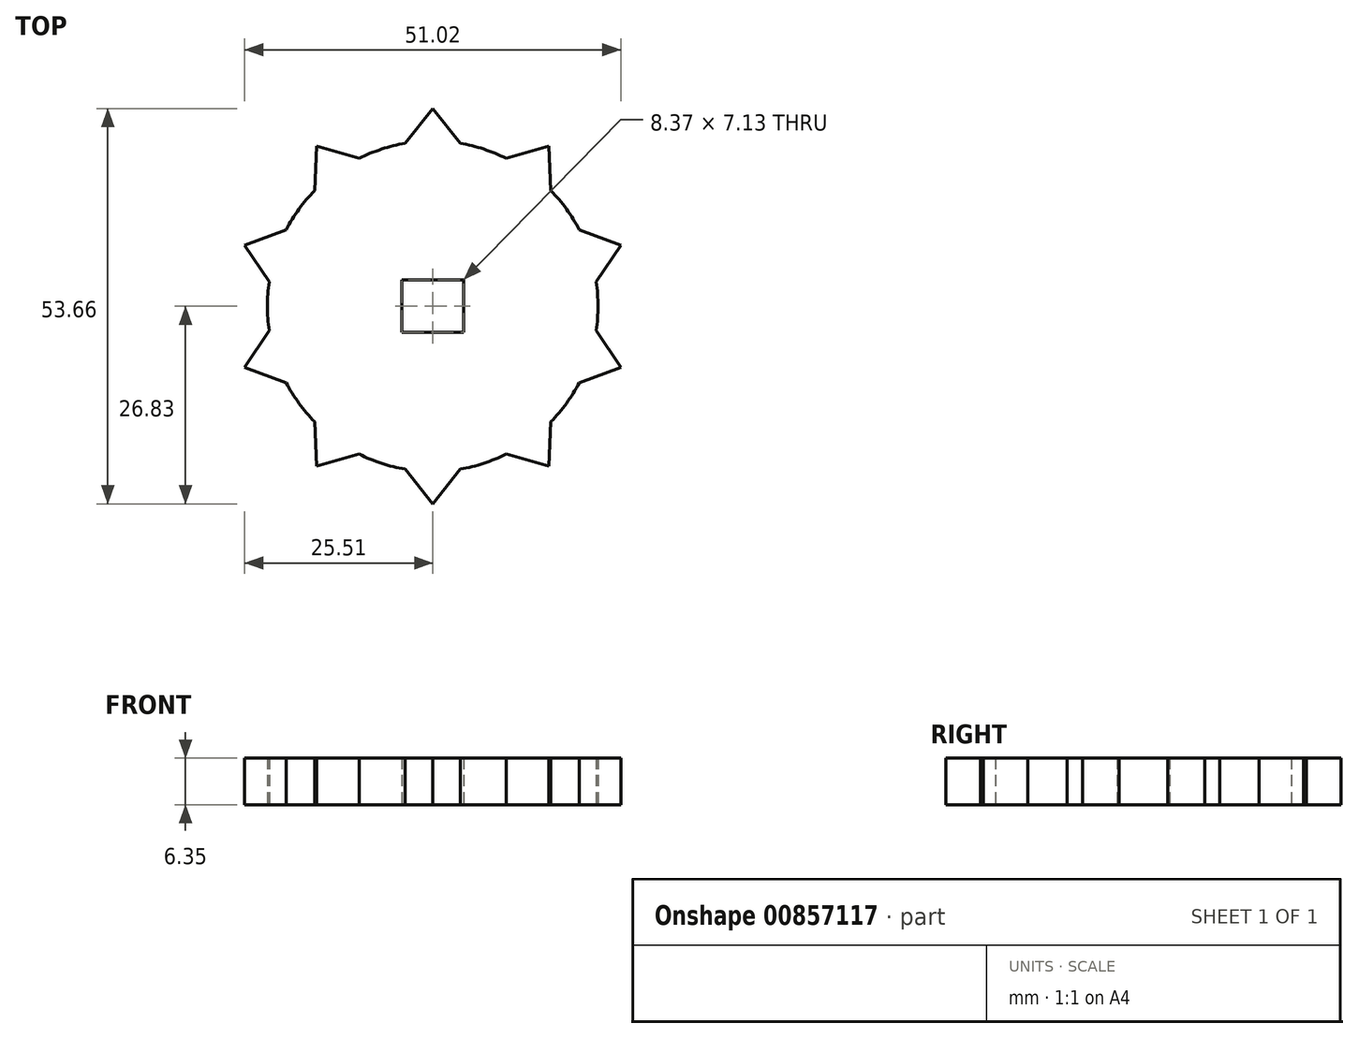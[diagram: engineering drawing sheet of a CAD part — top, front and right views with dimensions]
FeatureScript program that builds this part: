
annotation { "Feature Type Name" : "Feature", "Feature Type Description" : "" }
export const myFeature = defineFeature(function(context is Context, id is Id, definition is map)
    precondition{}
    {
        {
            var Q0;
            Q0=qCreatedBy(makeId("Top.planeOp"),FACE);
            var sketch = newSketch(context, id + "F0", { "sketchPlane" : qUnion([Q0])});
            skCircle(sketch, "E0", {"center": v(0, 0) * mm, "radius": 22.42 * mm});
            skCircle(sketch, "E1", {"center": v(0, 0) * mm, "radius": 8.67 * mm});
            skLineSegment(sketch, "E2.bottom", {"start": v(4.19, -3.57) * mm, "end": v(-4.19, -3.57) * mm});
            skLineSegment(sketch, "E2.top", {"start": v(4.19, 3.57) * mm, "end": v(-4.19, 3.57) * mm});
            skLineSegment(sketch, "E2.left", {"start": v(4.19, -3.57) * mm, "end": v(4.19, 3.57) * mm});
            skLineSegment(sketch, "E2.right", {"start": v(-4.19, -3.57) * mm, "end": v(-4.19, 3.57) * mm});
            skLineSegment(sketch, "E3", {"start": v(-3.72, 22.1) * mm, "end": v(0, 26.83) * mm});
            skLineSegment(sketch, "E4", {"start": v(0, 26.83) * mm, "end": v(3.72, 22.1) * mm});
            skLineSegment(sketch, "E5.1.0", {"start": v(-16, 15.7) * mm, "end": v(-15.77, 21.7) * mm});
            skLineSegment(sketch, "E5.1.1", {"start": v(-15.77, 21.7) * mm, "end": v(-9.98, 20.08) * mm});
            skLineSegment(sketch, "E5.2.0", {"start": v(-22.18, 3.29) * mm, "end": v(-25.51, 8.29) * mm});
            skLineSegment(sketch, "E5.2.1", {"start": v(-25.51, 8.29) * mm, "end": v(-19.88, 10.37) * mm});
            skLineSegment(sketch, "E5.3.0", {"start": v(-19.88, -10.37) * mm, "end": v(-25.51, -8.29) * mm});
            skLineSegment(sketch, "E5.3.1", {"start": v(-25.51, -8.29) * mm, "end": v(-22.18, -3.29) * mm});
            skLineSegment(sketch, "E5.4.0", {"start": v(-9.98, -20.08) * mm, "end": v(-15.77, -21.7) * mm});
            skLineSegment(sketch, "E5.4.1", {"start": v(-15.77, -21.7) * mm, "end": v(-16, -15.7) * mm});
            skLineSegment(sketch, "E5.5.0", {"start": v(3.72, -22.1) * mm, "end": v(0, -26.83) * mm});
            skLineSegment(sketch, "E5.5.1", {"start": v(0, -26.83) * mm, "end": v(-3.72, -22.1) * mm});
            skLineSegment(sketch, "E5.6.0", {"start": v(16, -15.7) * mm, "end": v(15.77, -21.7) * mm});
            skLineSegment(sketch, "E5.6.1", {"start": v(15.77, -21.7) * mm, "end": v(9.98, -20.08) * mm});
            skLineSegment(sketch, "E5.7.0", {"start": v(22.18, -3.29) * mm, "end": v(25.51, -8.29) * mm});
            skLineSegment(sketch, "E5.7.1", {"start": v(25.51, -8.29) * mm, "end": v(19.88, -10.37) * mm});
            skLineSegment(sketch, "E5.8.0", {"start": v(19.88, 10.37) * mm, "end": v(25.51, 8.29) * mm});
            skLineSegment(sketch, "E5.8.1", {"start": v(25.51, 8.29) * mm, "end": v(22.18, 3.29) * mm});
            skLineSegment(sketch, "E5.9.0", {"start": v(9.98, 20.08) * mm, "end": v(15.77, 21.7) * mm});
            skLineSegment(sketch, "E5.9.1", {"start": v(15.77, 21.7) * mm, "end": v(16, 15.7) * mm});
            skSolve(sketch);
        }
        {
            var Q0;
            Q0=makeQuery(id+"F0.imprint","IMPRINT",FACE,{"disambiguationData":[TD([[makeQuery(id+"F0.imprint","IMPRINT",EDGE,{"derivedFrom":sQuery(id+"F0.wireOp",EDGE,"E1")}),-1.0]])]});
            var Q1;
            {var subQ0=sQuery(id+"F0.wireOp",EDGE,"E5.1.0");Q1=makeQuery(id+"F0.imprint","IMPRINT",FACE,{"disambiguationData":[TD([[makeQuery(id+"F0.imprint","IMPRINT",EDGE,{"derivedFrom":subQ0}),-1.0]])]});}
            var Q2;
            {var subQ0=sQuery(id+"F0.wireOp",EDGE,"E3");Q2=makeQuery(id+"F0.imprint","IMPRINT",FACE,{"disambiguationData":[TD([[makeQuery(id+"F0.imprint","IMPRINT",EDGE,{"derivedFrom":subQ0}),-1.0]])]});}
            var Q3;
            {var subQ0=sQuery(id+"F0.wireOp",EDGE,"E5.9.0");Q3=makeQuery(id+"F0.imprint","IMPRINT",FACE,{"disambiguationData":[TD([[makeQuery(id+"F0.imprint","IMPRINT",EDGE,{"derivedFrom":subQ0}),-1.0]])]});}
            var Q4;
            {var subQ0=sQuery(id+"F0.wireOp",EDGE,"E5.8.0");Q4=makeQuery(id+"F0.imprint","IMPRINT",FACE,{"disambiguationData":[TD([[makeQuery(id+"F0.imprint","IMPRINT",EDGE,{"derivedFrom":subQ0}),-1.0]])]});}
            var Q5;
            {var subQ0=sQuery(id+"F0.wireOp",EDGE,"E5.7.0");Q5=makeQuery(id+"F0.imprint","IMPRINT",FACE,{"disambiguationData":[TD([[makeQuery(id+"F0.imprint","IMPRINT",EDGE,{"derivedFrom":subQ0}),-1.0]])]});}
            var Q6;
            {var subQ0=sQuery(id+"F0.wireOp",EDGE,"E5.6.0");Q6=makeQuery(id+"F0.imprint","IMPRINT",FACE,{"disambiguationData":[TD([[makeQuery(id+"F0.imprint","IMPRINT",EDGE,{"derivedFrom":subQ0}),-1.0]])]});}
            var Q7;
            {var subQ0=sQuery(id+"F0.wireOp",EDGE,"E5.5.0");Q7=makeQuery(id+"F0.imprint","IMPRINT",FACE,{"disambiguationData":[TD([[makeQuery(id+"F0.imprint","IMPRINT",EDGE,{"derivedFrom":subQ0}),-1.0]])]});}
            var Q8;
            {var subQ0=sQuery(id+"F0.wireOp",EDGE,"E5.4.0");Q8=makeQuery(id+"F0.imprint","IMPRINT",FACE,{"disambiguationData":[TD([[makeQuery(id+"F0.imprint","IMPRINT",EDGE,{"derivedFrom":subQ0}),-1.0]])]});}
            var Q9;
            {var subQ0=sQuery(id+"F0.wireOp",EDGE,"E5.3.0");Q9=makeQuery(id+"F0.imprint","IMPRINT",FACE,{"disambiguationData":[TD([[makeQuery(id+"F0.imprint","IMPRINT",EDGE,{"derivedFrom":subQ0}),-1.0]])]});}
            var Q10;
            {var subQ0=sQuery(id+"F0.wireOp",EDGE,"E5.2.0");Q10=makeQuery(id+"F0.imprint","IMPRINT",FACE,{"disambiguationData":[TD([[makeQuery(id+"F0.imprint","IMPRINT",EDGE,{"derivedFrom":subQ0}),-1.0]])]});}
            var Q11;
            Q11=makeQuery(id+"F0.imprint","IMPRINT",FACE,{"disambiguationData":[TD([[makeQuery(id+"F0.imprint","IMPRINT",EDGE,{"derivedFrom":sQuery(id+"F0.wireOp",EDGE,"E1")}),1.0]])]});
            extrude(context, id + "F1", {"entities" : qUnion([Q0, Q1, Q2, Q3, Q4, Q5, Q6, Q7, Q8, Q9, Q10, Q11]), "depth" : 6.35 * mm, "offsetDistance" : 25.4 * mm});
        }
    });
